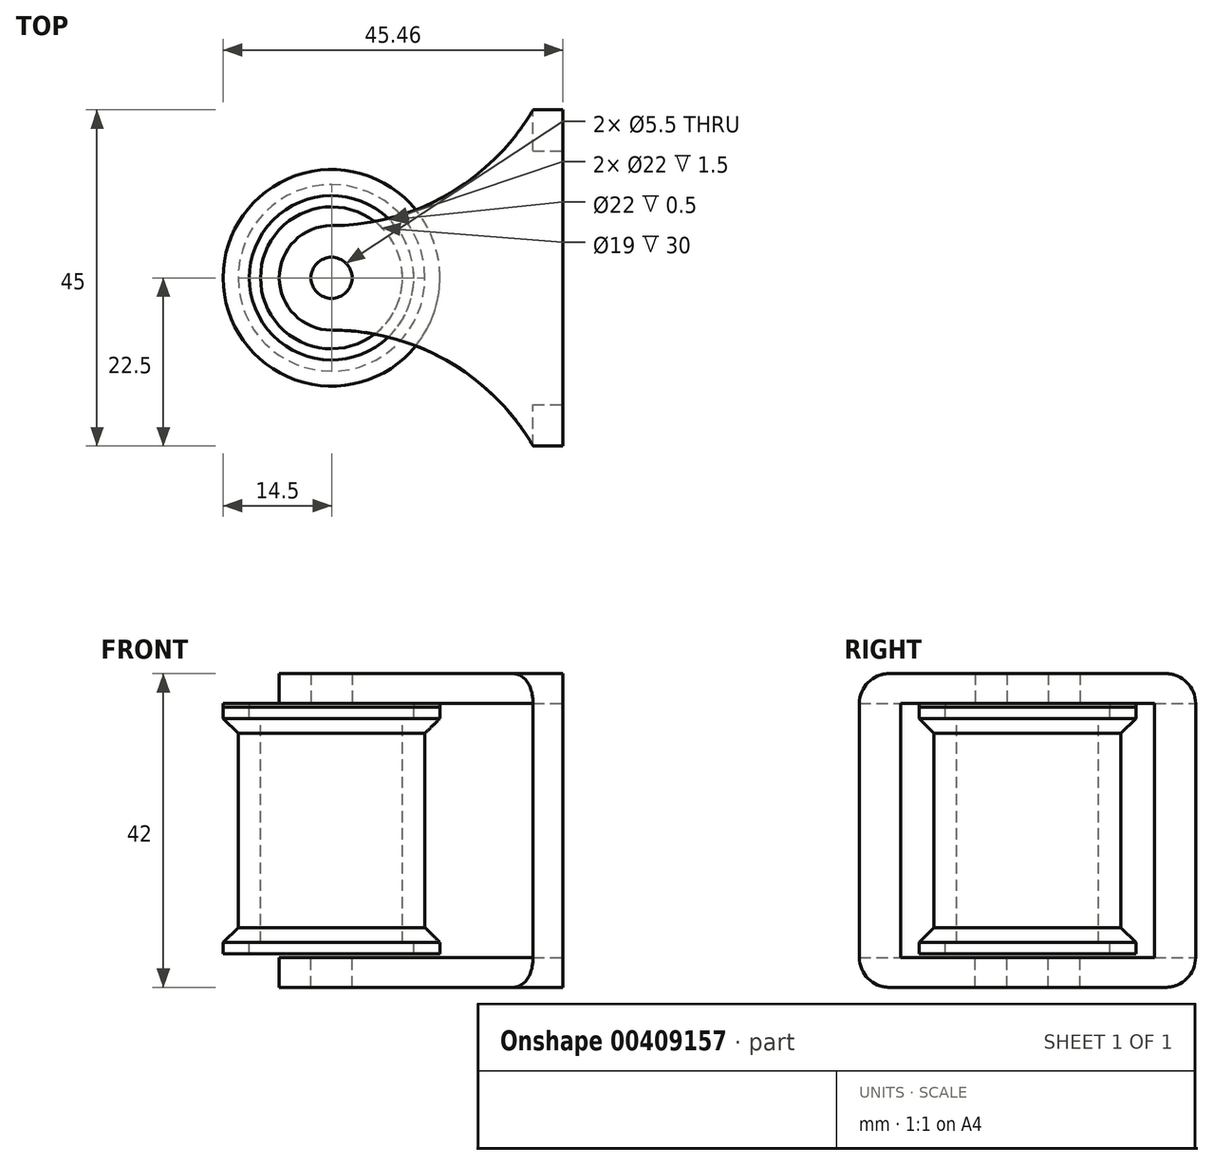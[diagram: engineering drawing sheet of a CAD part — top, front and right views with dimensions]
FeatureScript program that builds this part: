
annotation { "Feature Type Name" : "Feature", "Feature Type Description" : "" }
export const myFeature = defineFeature(function(context is Context, id is Id, definition is map)
    precondition{}
    {
        {
            var Q0;
            Q0=qCreatedBy(makeId("Front.planeOp"),FACE);
            var sketch = newSketch(context, id + "F0", { "sketchPlane" : qUnion([Q0])});
            skLineSegment(sketch, "E0", {"start": v(11, 16.5) * mm, "end": v(14.5, 16.5) * mm});
            skLineSegment(sketch, "E1", {"start": v(14.5, 16.5) * mm, "end": v(14.5, 15) * mm});
            skLineSegment(sketch, "E2", {"start": v(14.5, 15) * mm, "end": v(12.5, 13) * mm});
            skLineSegment(sketch, "E3", {"start": v(12.5, 13) * mm, "end": v(12.5, 0) * mm});
            skLineSegment(sketch, "E4", {"start": v(11, 16.5) * mm, "end": v(11, 15) * mm});
            skLineSegment(sketch, "E5", {"start": v(11, 15) * mm, "end": v(9.5, 15) * mm});
            skLineSegment(sketch, "E6", {"start": v(9.5, 15) * mm, "end": v(9.5, 0) * mm});
            skLineSegment(sketch, "E7", {"start": v(0, 34.74) * mm, "end": v(0, -34.32) * mm, "construction": true});
            skLineSegment(sketch, "E8.MirrorCS", {"start": v(14.5, -15) * mm, "end": v(12.5, -13) * mm});
            skLineSegment(sketch, "E9.MirrorCS", {"start": v(11, -16.5) * mm, "end": v(11, -15) * mm});
            skLineSegment(sketch, "E10.MirrorCS", {"start": v(11, -15) * mm, "end": v(9.5, -15) * mm});
            skLineSegment(sketch, "E11.MirrorCS", {"start": v(11, -16.5) * mm, "end": v(14.5, -16.5) * mm});
            skLineSegment(sketch, "E12.MirrorCS", {"start": v(14.5, -16.5) * mm, "end": v(14.5, -15) * mm});
            skLineSegment(sketch, "E13.MirrorCS", {"start": v(9.5, -15) * mm, "end": v(9.5, 0) * mm});
            skLineSegment(sketch, "E14.MirrorCS", {"start": v(12.5, -13) * mm, "end": v(12.5, 0) * mm});
            skSolve(sketch);
        }
        {
            var Q0;
            Q0=makeQuery(id+"F0.imprint","IMPRINT",FACE,{"disambiguationData":[TD([[makeQuery(id+"F0.imprint","IMPRINT",EDGE,{"derivedFrom":sQuery(id+"F0.wireOp",EDGE,"E0")}),-1.0]])]});
            var Q1;
            Q1=sQuery(id+"F0.wireOp",EDGE,"E7");
            revolve(context, id + "F1", {"entities" : qUnion([Q0]), "axis" : qUnion([Q1]), "revolveType" : RevolveType.FULL});
        }
        {
            var Q0;
            Q0=makeQuery(id+"F1.opRevolve","SWEPT_FACE",FACE,{"disambiguationData":[OSD([sQuery(id+"F0.wireOp",EDGE,"E0")])]});
            extrude(context, id + "F2", {"entities" : qUnion([Q0]), "depth" : 0.5 * mm, "offsetDistance" : 25 * mm});
        }
        {
            var Q0;
            Q0=makeQuery(id+"F2.opExtrude","CAP_FACE",FACE,{"disambiguationData":[OSD([sQuery(id+"F0.wireOp",EDGE,"E0")])],"isStart":false});
            var sketch = newSketch(context, id + "F3", { "sketchPlane" : qUnion([Q0])});
            skLineSegment(sketch, "E15", {"start": v(26.96, 0) * mm, "end": v(26.96, 22.5) * mm});
            skLineSegment(sketch, "E16", {"start": v(26.96, 22.5) * mm, "end": v(30.96, 22.5) * mm});
            skLineSegment(sketch, "E17", {"start": v(30.96, 22.5) * mm, "end": v(30.96, 0) * mm});
            skCircle(sketch, "E18", {"center": v(0, 0) * mm, "radius": 2.75 * mm});
            skArc(sketch, "E19", {"start": v(0, 7) * mm, "mid": v(-4.95, 4.95) * mm, "end": v(-7, 0) * mm});
            skLineSegment(sketch, "E20.MirrorCS", {"start": v(30.96, -22.5) * mm, "end": v(30.96, 0) * mm});
            skLineSegment(sketch, "E21.MirrorCS", {"start": v(26.96, -22.5) * mm, "end": v(30.96, -22.5) * mm});
            skLineSegment(sketch, "E22.MirrorCS", {"start": v(26.96, 0) * mm, "end": v(26.96, -22.5) * mm});
            skArc(sketch, "E23.MirrorCS", {"start": v(0, -7) * mm, "mid": v(-4.95, -4.95) * mm, "end": v(-7, 0) * mm});
            skLineSegment(sketch, "E24.bottom", {"start": v(50.96, -30) * mm, "end": v(30.96, -30) * mm, "construction": true});
            skLineSegment(sketch, "E24.top", {"start": v(50.96, 30) * mm, "end": v(30.96, 30) * mm, "construction": true});
            skLineSegment(sketch, "E24.left", {"start": v(50.96, -30) * mm, "end": v(50.96, 30) * mm, "construction": true});
            skLineSegment(sketch, "E24.right", {"start": v(30.96, -30) * mm, "end": v(30.96, 30) * mm, "construction": true});
            skPoint(sketch, "E24.middle", {"position": v(40.96, 0) * mm});
            skLineSegment(sketch, "E25", {"start": v(-0.59, 12.36) * mm, "end": v(28.22, 29) * mm, "construction": true});
            skCircle(sketch, "E26", {"center": v(30.96, 30) * mm, "radius": 0.5 * mm, "construction": true});
            skArc(sketch, "E27", {"start": v(0, 7) * mm, "mid": v(15.55, 11.15) * mm, "end": v(26.96, 22.5) * mm});
            skArc(sketch, "E28.MirrorCS", {"start": v(0, -7) * mm, "mid": v(15.55, -11.15) * mm, "end": v(26.96, -22.5) * mm});
            skSolve(sketch);
        }
        {
            var Q0;
            {var subQ4=sQuery(id+"F3.wireOp",EDGE,"E19");Q0=makeQuery(id+"F3.imprint","IMPRINT",FACE,{"disambiguationData":[TD([[makeQuery(id+"F3.imprint","IMPRINT",EDGE,{"derivedFrom":subQ4}),1.0]])]});}
            var Q1;
            {var subQ4=sQuery(id+"F3.wireOp",EDGE,"E15");Q1=makeQuery(id+"F3.imprint","IMPRINT",FACE,{"disambiguationData":[TD([[makeQuery(id+"F3.imprint","IMPRINT",EDGE,{"derivedFrom":subQ4}),1.0]])]});}
            var Q2;
            {var subQ0=sQuery(id+"F3.wireOp",EDGE,"EvobU9dw-gI2S-dZkZ-4M56-SvZedtwLsl3Y");var subQ1=sQuery(id+"F0.wireOp",EDGE,"E0");var subQ2=makeQuery(id+"F2.opExtrude","CAP_EDGE",EDGE,{"disambiguationData":[OSD([subQ1,sQuery(id+"F0.wireOp",EDGE,"E1")])],"isStart":false});var subQ3=makeQuery(id+"F3.imprint","INTERSECT",VERTEX,{"derivedFrom":[subQ2,subQ0]});Q2=makeQuery(id+"F3.imprint","IMPRINT",FACE,{"disambiguationData":[TD([[makeQuery(id+"F3.imprint","IMPRINT",EDGE,{"disambiguationData":[TD([[subQ3,-1.0]])],"derivedFrom":subQ0}),1.0]])]});}
            var Q3;
            Q3=makeQuery(id+"F3.imprint","IMPRINT",FACE,{"disambiguationData":[TD([[makeQuery(id+"F3.imprint","IMPRINT",EDGE,{"derivedFrom":sQuery(id+"F3.wireOp",EDGE,"E15")}),-1.0]])]});
            var Q4;
            {var subQ0=sQuery(id+"F3.wireOp",EDGE,"f2d5ea2f-3cbe-4428-b8be-76cd246570a34.MirrorCS");var subQ1=sQuery(id+"F3.wireOp",EDGE,"E22.MirrorCS");var subQ2=makeQuery(id+"F3.imprint","INTERSECT",VERTEX,{"derivedFrom":[sQuery(id+"F3.wireOp",EDGE,"E21.MirrorCS"),subQ1,subQ0]});Q4=makeQuery(id+"F3.imprint","IMPRINT",FACE,{"disambiguationData":[TD([[makeQuery(id+"F3.imprint","IMPRINT",EDGE,{"disambiguationData":[TD([[subQ2,1.0]])],"derivedFrom":subQ1}),-1.0]])]});}
            var Q5;
            {var subQ0=sQuery(id+"F3.wireOp",EDGE,"E16");Q5=makeQuery(id+"F3.imprint","IMPRINT",FACE,{"disambiguationData":[TD([[makeQuery(id+"F3.imprint","IMPRINT",EDGE,{"derivedFrom":subQ0}),-1.0]])]});}
            var Q6;
            {var subQ0=sQuery(id+"F3.wireOp",EDGE,"E27");var subQ1=sQuery(id+"F0.wireOp",EDGE,"E0");var subQ2=makeQuery(id+"F2.opExtrude","CAP_EDGE",EDGE,{"disambiguationData":[OSD([subQ1,sQuery(id+"F0.wireOp",EDGE,"E1")])],"isStart":false});var subQ3=makeQuery(id+"F3.imprint","INTERSECT",VERTEX,{"derivedFrom":[subQ2,subQ0]});Q6=makeQuery(id+"F3.imprint","IMPRINT",FACE,{"disambiguationData":[TD([[makeQuery(id+"F3.imprint","IMPRINT",EDGE,{"disambiguationData":[TD([[subQ3,1.0]])],"derivedFrom":subQ0}),-1.0]])]});}
            extrude(context, id + "F4", {"entities" : qUnion([Q0, Q1, Q2, Q3, Q4, Q5, Q6]), "depth" : 4 * mm, "offsetDistance" : 25 * mm});
        }
        {
            var Q0;
            Q0=makeQuery(id+"F4.opExtrude","SWEPT_BODY",BODY,{"disambiguationData":[OSD([sQuery(id+"F3.wireOp",EDGE,"E16"),sQuery(id+"F3.wireOp",EDGE,"E17"),sQuery(id+"F3.wireOp",EDGE,"EvobU9dw-gI2S-dZkZ-4M56-SvZedtwLsl3Y"),sQuery(id+"F3.wireOp",EDGE,"E19"),sQuery(id+"F3.wireOp",EDGE,"E20.MirrorCS"),sQuery(id+"F3.wireOp",EDGE,"E18"),sQuery(id+"F3.wireOp",EDGE,"E21.MirrorCS"),sQuery(id+"F3.wireOp",EDGE,"f2d5ea2f-3cbe-4428-b8be-76cd246570a34.MirrorCS"),sQuery(id+"F3.wireOp",EDGE,"E23.MirrorCS")])]});
            var Q1;
            Q1=qCreatedBy(makeId("Top.planeOp"),FACE);
            mirror(context, id + "F5", {"entities" : qUnion([Q0]), "mirrorPlane" : qUnion([Q1])});
        }
        {
            var Q0;
            {var subQ0=sQuery(id+"F3.wireOp",EDGE,"E16");Q0=makeQuery(id+"F3.imprint","IMPRINT",FACE,{"disambiguationData":[TD([[makeQuery(id+"F3.imprint","IMPRINT",EDGE,{"derivedFrom":subQ0}),-1.0]])]});}
            extrude(context, id + "F6", {"entities" : qUnion([Q0]), "operationType" : NewBodyOperationType.ADD, "endBound" : BoundingType.UP_TO_NEXT, "oppositeDirection" : true, "depth" : 25 * mm, "offsetDistance" : 25 * mm});
        }
        {
            var Q0;
            Q0=makeQuery(id+"F4.opExtrude","CAP_EDGE",EDGE,{"disambiguationData":[OSD([sQuery(id+"F3.wireOp",EDGE,"E16")])],"isStart":false});
            var Q1;
            Q1=makeQuery(id+"F5.opPattern","COPY",EDGE,{"derivedFrom":makeQuery(id+"F4.opExtrude","CAP_EDGE",EDGE,{"disambiguationData":[OSD([sQuery(id+"F3.wireOp",EDGE,"E16")])],"isStart":false}),"instanceName":"1"});
            var Q2;
            Q2=makeQuery(id+"F5.opPattern","COPY",EDGE,{"derivedFrom":makeQuery(id+"F4.opExtrude","CAP_EDGE",EDGE,{"disambiguationData":[OSD([sQuery(id+"F3.wireOp",EDGE,"E21.MirrorCS")])],"isStart":false}),"instanceName":"1"});
            var Q3;
            Q3=makeQuery(id+"F4.opExtrude","CAP_EDGE",EDGE,{"disambiguationData":[OSD([sQuery(id+"F3.wireOp",EDGE,"E21.MirrorCS")])],"isStart":false});
            var Q4;
            Q4=makeQuery(id+"F9.boolean.opBoolean","COPY",EDGE,{"derivedFrom":makeQuery(id+"F9.opExtrude","SWEPT_EDGE",EDGE,{"disambiguationData":[OSD([sQuery(id+"F8.wireOp",EDGE,"E29.top"),sQuery(id+"F8.wireOp",EDGE,"E29.left")])]})});
            var Q5;
            Q5=makeQuery(id+"F9.boolean.opBoolean","COPY",EDGE,{"derivedFrom":makeQuery(id+"F9.opExtrude","SWEPT_EDGE",EDGE,{"disambiguationData":[OSD([sQuery(id+"F8.wireOp",EDGE,"E29.top"),sQuery(id+"F8.wireOp",EDGE,"E29.right")])]})});
            var Q6;
            Q6=makeQuery(id+"F9.boolean.opBoolean","COPY",EDGE,{"derivedFrom":makeQuery(id+"F9.opExtrude","SWEPT_EDGE",EDGE,{"disambiguationData":[OSD([sQuery(id+"F8.wireOp",EDGE,"E29.bottom"),sQuery(id+"F8.wireOp",EDGE,"E29.left")])]})});
            var Q7;
            Q7=makeQuery(id+"F9.boolean.opBoolean","COPY",EDGE,{"derivedFrom":makeQuery(id+"F9.opExtrude","SWEPT_EDGE",EDGE,{"disambiguationData":[OSD([sQuery(id+"F8.wireOp",EDGE,"E29.bottom"),sQuery(id+"F8.wireOp",EDGE,"E29.right")])]})});
            fillet(context, id + "F7", {"entities" : qUnion([Q0, Q1, Q2, Q3, Q4, Q5, Q6, Q7]), "radius" : 4 * mm, "tangentPropagation" : true, "allowEdgeOverflow" : false});
        }
        {
            var Q0;
            {var subQ0=sQuery(id+"F3.wireOp",EDGE,"E20.MirrorCS");var subQ1=sQuery(id+"F3.wireOp",EDGE,"E17");var subQ2=makeQuery(id+"F4.opExtrude","SWEPT_FACE",FACE,{"disambiguationData":[OSD([subQ1,subQ0])]});Q0=makeQuery(id+"F6.boolean.opBoolean","MERGE",FACE,{"derivedFrom":[subQ2,makeQuery(id+"F5.opPattern","COPY",FACE,{"derivedFrom":subQ2,"instanceName":"1"}),makeQuery(id+"F6.opExtrude","SWEPT_FACE",FACE,{"disambiguationData":[OSD([subQ1,subQ0])]})]});}
            var sketch = newSketch(context, id + "F8", { "sketchPlane" : qUnion([Q0])});
            skLineSegment(sketch, "E29.bottom", {"start": v(17, -17) * mm, "end": v(-17, -17) * mm});
            skLineSegment(sketch, "E29.top", {"start": v(17, 17) * mm, "end": v(-17, 17) * mm});
            skLineSegment(sketch, "E29.left", {"start": v(17, -17) * mm, "end": v(17, 17) * mm});
            skLineSegment(sketch, "E29.right", {"start": v(-17, -17) * mm, "end": v(-17, 17) * mm});
            skPoint(sketch, "E29.middle", {"position": v(0, 0) * mm});
            skSolve(sketch);
        }
        {
            var Q0;
            Q0=makeQuery(id+"F8.imprint","IMPRINT",FACE,{"disambiguationData":[TD([[makeQuery(id+"F8.imprint","IMPRINT",EDGE,{"derivedFrom":sQuery(id+"F8.wireOp",EDGE,"E29.bottom")}),-1.0]])]});
            var Q1;
            Q1=makeQuery(id+"F6.opExtrude","SWEPT_FACE",FACE,{"disambiguationData":[OSD([sQuery(id+"F3.wireOp",EDGE,"E15"),sQuery(id+"F3.wireOp",EDGE,"E22.MirrorCS")])]});
            extrude(context, id + "F9", {"entities" : qUnion([Q0]), "operationType" : NewBodyOperationType.REMOVE, "endBound" : BoundingType.UP_TO_SURFACE, "oppositeDirection" : true, "depth" : 25 * mm, "endBoundEntityFace" : qUnion([Q1]), "offsetDistance" : 25 * mm});
        }
    });
